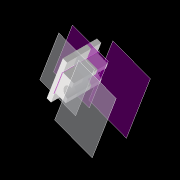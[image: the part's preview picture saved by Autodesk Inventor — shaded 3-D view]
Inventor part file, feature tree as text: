
AUTODESK INVENTOR PART (.ipt)
format: ipt  version: 2021 (Build 250183000, 183)  size: 153,600 bytes
history: native  units: mm
features: plane x5, sketch x5, reference x5, extrude x4, other x4, hole x1
ambient origin geometry x8: Origin, YZ Plane, XZ Plane, XY Plane, X Axis, Y Axis, Z Axis, Center Point
bodies: Solid1 (feature_tree), Solid2 (feature_tree), Solid3 (feature_tree)
feature tree (24):
  plane  "Work Plane1"
  sketch  "Sketch1"  dims[d1=180.0deg d2=50.0mm]
  plane  "Work Plane2"
  extrude  "Extrusion1"  Depth=50.0mm
  plane  "Work Plane3"
  extrude  "Extrusion2"  Depth=50.0mm
  plane  "Work Plane5"
  plane  "Work Plane6"
  extrude  "Extrusion3"  TaperAngle=0.0deg  [1 undecoded]
  extrude  "Extrusion4"  [1 undecoded]
  hole  "Hole1"  [1 undecoded]
  reference  "Reference1"
  sketch  "Sketch2"  dims[d3=100.0mm d4=50.0mm]
  reference  "Reference2"
  reference  "Reference3"
  reference  "Reference5"
  sketch  "Sketch3"  dims[d5=10.0mm d6=0.0mm d7=0.0mm]
  sketch  "Sketch4"  dims[d8=20.0mm d9=0.0mm d12=-45.0mm]
  sketch  "Sketch5"  dims[d13=-45.0mm d14=5.0mm d15=100.0mm d16=11.0mm d17=26.9875mm d18=20.0mm d19=0.0mm d20=30.0mm d21=27.2875mm d22=10.0mm d23=0.0mm d24=0.0mm d25=10.0mm d26=6.0mm d27=4.0mm d28=2.0mm d29=90.0deg d30=10.0mm d31=20.594885mm]
  reference  "Reference6"
  other  "Subensamble_mesa.iam"
  other  "Tubo-2_1_8:1"
  other  "Base soporte tubos:2"
  other  "Eje roscado base soporte tubo:1"
note: 3 required parameter values undecoded (feature->parameter linkage not recoverable at this tier; creation-order binding heuristic only, values carry confidence <= 0.55)
